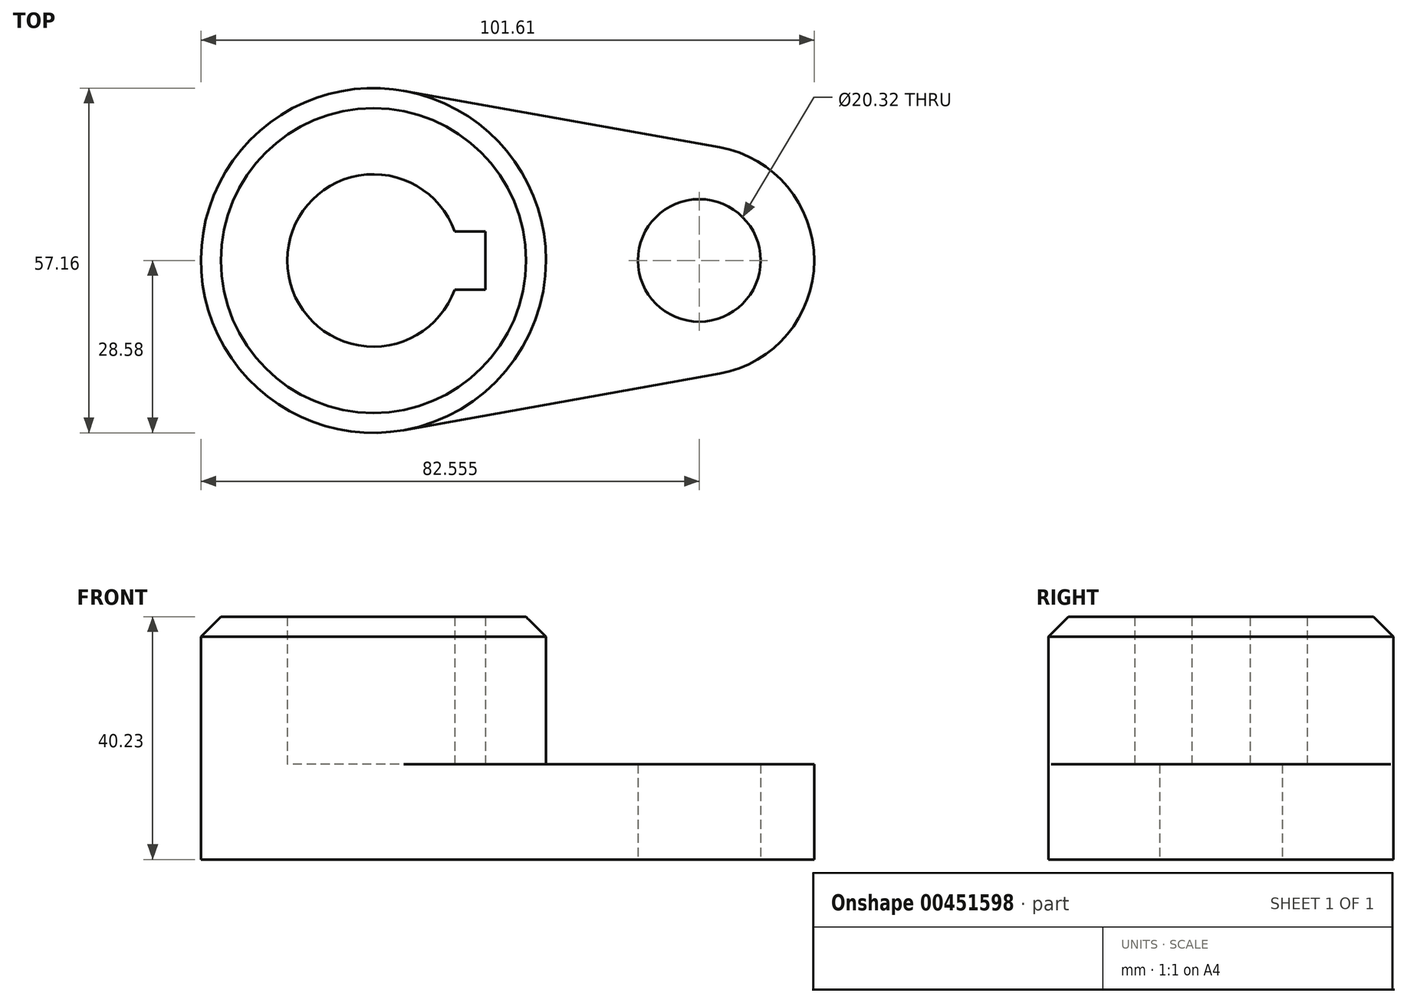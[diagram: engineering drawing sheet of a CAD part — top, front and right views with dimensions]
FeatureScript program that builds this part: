
annotation { "Feature Type Name" : "Feature", "Feature Type Description" : "" }
export const myFeature = defineFeature(function(context is Context, id is Id, definition is map)
    precondition{}
    {
        {
            var Q0;
            Q0=qCreatedBy(makeId("Top.planeOp"),FACE);
            var sketch = newSketch(context, id + "F0", { "sketchPlane" : qUnion([Q0])});
            skArc(sketch, "E0", {"start": v(5.04, 28.13) * mm, "mid": v(-28.58, 0) * mm, "end": v(5.04, -28.13) * mm});
            skArc(sketch, "E1", {"start": v(57.34, -18.75) * mm, "mid": v(73.03, 0) * mm, "end": v(57.34, 18.75) * mm});
            skLineSegment(sketch, "E2", {"start": v(5.04, 28.13) * mm, "end": v(57.34, 18.75) * mm});
            skLineSegment(sketch, "E3", {"start": v(5.04, -28.13) * mm, "end": v(57.34, -18.75) * mm});
            skCircle(sketch, "E4", {"center": v(53.98, 0) * mm, "radius": 10.16 * mm});
            skSolve(sketch);
        }
        {
            var Q0;
            Q0=makeQuery(id+"F0.imprint","IMPRINT",FACE,{"disambiguationData":[TD([[makeQuery(id+"F0.imprint","IMPRINT",EDGE,{"derivedFrom":sQuery(id+"F0.wireOp",EDGE,"E0")}),1.0]])]});
            extrude(context, id + "F1", {"entities" : qUnion([Q0]), "depth" : 15.77 * mm});
        }
        {
            var Q0;
            Q0=qCreatedBy(makeId("Top.planeOp"),FACE);
            var sketch = newSketch(context, id + "F2", { "sketchPlane" : qUnion([Q0])});
            skArc(sketch, "E5", {"start": v(13.45, 4.83) * mm, "mid": v(-14.29, 0) * mm, "end": v(13.45, -4.83) * mm});
            skLineSegment(sketch, "E6", {"start": v(18.53, 4.83) * mm, "end": v(18.53, -4.83) * mm});
            skLineSegment(sketch, "E7", {"start": v(18.53, 4.83) * mm, "end": v(13.45, 4.83) * mm});
            skLineSegment(sketch, "E8", {"start": v(18.53, -4.83) * mm, "end": v(13.45, -4.83) * mm});
            skCircle(sketch, "E9", {"center": v(0, 0) * mm, "radius": 28.58 * mm});
            skSolve(sketch);
        }
        {
            var Q0;
            Q0=makeQuery(id+"F2.imprint","IMPRINT",FACE,{"disambiguationData":[TD([[makeQuery(id+"F2.imprint","IMPRINT",EDGE,{"derivedFrom":sQuery(id+"F2.wireOp",EDGE,"E5")}),-1.0]])]});
            extrude(context, id + "F3", {"entities" : qUnion([Q0]), "operationType" : NewBodyOperationType.ADD, "depth" : 40.23 * mm});
        }
        {
            var Q0;
            Q0=makeQuery(id+"F3.opExtrude","CAP_EDGE",EDGE,{"disambiguationData":[OSD([sQuery(id+"F2.wireOp",EDGE,"E9")])],"isStart":false});
            chamfer(context, id + "F4", {"entities" : qUnion([Q0]), "width" : 3.3 * mm, "tangentPropagation" : true});
        }
    });
